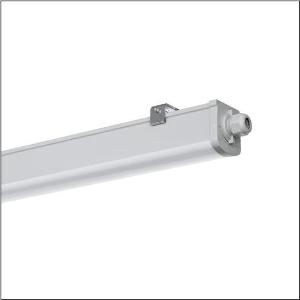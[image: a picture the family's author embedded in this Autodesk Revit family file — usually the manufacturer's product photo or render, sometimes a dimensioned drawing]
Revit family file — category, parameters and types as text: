
# Revit family: monsun_r__31_51fa20dk450b_5819
name_source: partatom
category: Lighting Fixtures
units: mm (PartAtom-declared; Revit-internal decimal feet)

## family parameters
Cut with Voids When Loaded = No
Host = Face
Light Source = No
Part Type = Normal
Room Calculation Point = No
Round Connector Dimension = Use Diameter
Shared = No

## types (1)
- Monsun® 31 (1 x LED, 5100 lm, 38 W, 4000K)
    Apparent Load = 38 VA
    CIE Flux Codes = 42 72 91 92 100
    Color Rendering = 80
    Color Temperature = 4000K
    Default Elevation = 1800 mm
    Description = Monsun® 31, damp-proof luminaire, primary optical cover: diffuser, of PC, frosted, light emission: direct distribution, primary light characteristic: symmetric, installation type: surface-mounted, LED, rated luminous flux: 5.100lm, luminous efficacy: 134lm/W, light colour: 840, colour temperature: 4000K, control gear: ECG, with terminal, 5+1-pole, max. 2.5mm², through-wiring: 3x 2.5mm² + 3x 1.5mm², mains connection: 220..240V, AC, 50/60Hz, rated input power: 38W, housing, luminaire housing, of PC, light grey (RAL 7035), length: 1.158mm, width: 68mm, height: 76mm, protection rating (complete): IP66, insulation class (complete): insulation class II (safety insulation), certification: CE, ENEC, UKCA, protection symbol: D, impact resistance: IK08, permissible operating ambient temperature: -20..+40°C, corresponds to IFS (International Featured Standards) requirements for safety and quality in the food industry, contact your sales advisor before using the luminaires in applications with unclear chemical exposure, large temperature fluctuations or condensation-forming humidity, packaging unit: 1 piece
    Height = 77 mm
    Lamp = 1 x LED
    Lamp Light Flux = 5100 lm
    Lamp Power = 38 W
    Lamp count = 1
    Length = 1218 mm
    Luminous efficacy = 134 lm/W
    Manufacturer = Siteco
    ModVariant = No
    Model = 51FA20DK450B
    Mounting Place = Ceiling
    Mounting Type = Surface mounted
    Number of Poles = 1
    OnlyDefault = Yes
    Power Factor = 1
    Product Name = Monsun® 31
    Product group = damp-proof luminaire
    ProductGroupID = 301
    Protection Class = Protection class II
    Protection Degree = IP 66
    RLX_Detail_Level = 1
    RLX_Emergency_Light_Flux = 0 lm
    RLX_Emergency_Type = 0
    RLX_Emergency_Type_DB = No
    RlxData = <blob elided: 32901 chars, md5=a97bfb98>
    Socket = socket
    Standby Power = 0 W
    System Light Flux = 5100 lm
    System Power = 38 W
    Type Comments = Product without accessories
    Type Image = l_1006174.jpg
    URL = http://relux.com
    VarID = ---
    Voltage = 0 V
    Weight = 0.00 kg
    Width = 69 mm

## geometry (parser evidence)
native form markers: Blend x4, Sweep x12
no freeform markers — native parametric forms only
